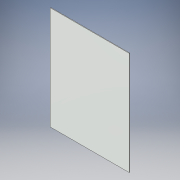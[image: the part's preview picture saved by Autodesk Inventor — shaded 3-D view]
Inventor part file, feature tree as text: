
AUTODESK INVENTOR PART (.ipt)
format: ipt  version: 2018 (Build 220112000, 112)  size: 93,696 bytes
history: native  units: in
note: dims shown in document units (in); Inventor stores cm internally (conversion verified against a paired STEP export)
features: extrude x1, sketch x1
ambient origin geometry x8: Origin, YZ Plane, XZ Plane, XY Plane, X Axis, Y Axis, Z Axis, Center Point
bodies: Solid1 (feature_tree)
feature tree (2):
  extrude  "Extrusion1"  Depth=22.25in
  sketch  "Sketch1"  dims[d0=17.0in d1=22.25in d2=0.125in d3=0.0in]
